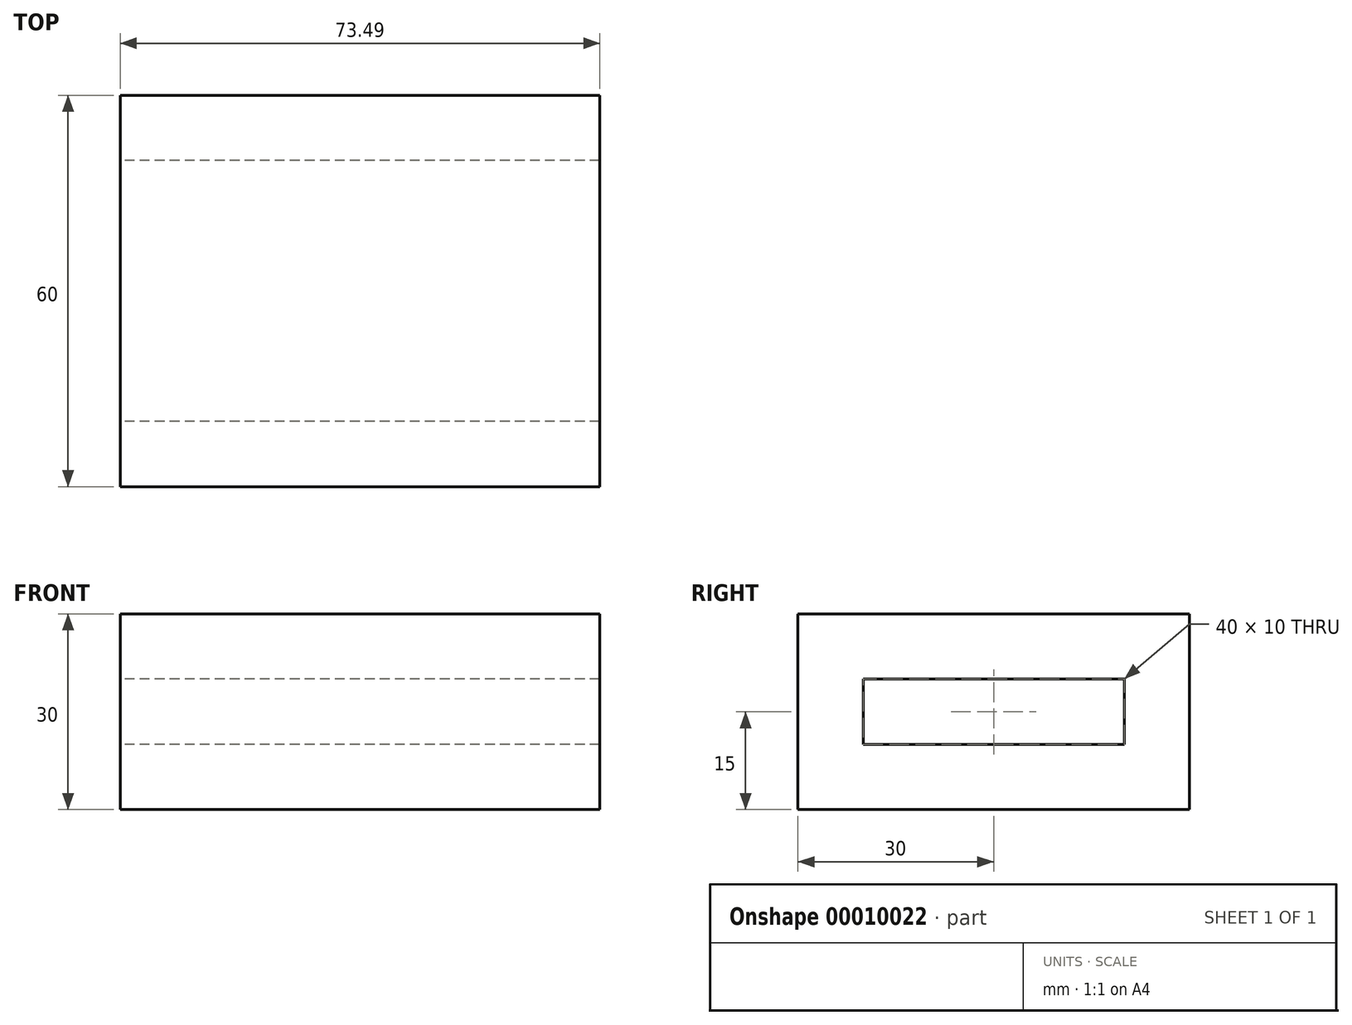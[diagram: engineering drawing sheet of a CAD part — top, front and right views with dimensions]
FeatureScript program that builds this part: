
annotation { "Feature Type Name" : "Feature", "Feature Type Description" : "" }
export const myFeature = defineFeature(function(context is Context, id is Id, definition is map)
    precondition{}
    {
        {
            var Q0;
            Q0=qCreatedBy(makeId("Right.planeOp"),FACE);
            var sketch = newSketch(context, id + "F0", { "sketchPlane" : qUnion([Q0])});
            skLineSegment(sketch, "E0.bottom", {"start": v(0, 0) * mm, "end": v(60, 0) * mm});
            skLineSegment(sketch, "E0.top", {"start": v(0, 30) * mm, "end": v(60, 30) * mm});
            skLineSegment(sketch, "E0.left", {"start": v(0, 0) * mm, "end": v(0, 30) * mm});
            skLineSegment(sketch, "E0.right", {"start": v(60, 0) * mm, "end": v(60, 30) * mm});
            skLineSegment(sketch, "E1.bottom", {"start": v(10, 20) * mm, "end": v(50, 20) * mm});
            skLineSegment(sketch, "E1.top", {"start": v(10, 10) * mm, "end": v(50, 10) * mm});
            skLineSegment(sketch, "E1.left", {"start": v(10, 20) * mm, "end": v(10, 10) * mm});
            skLineSegment(sketch, "E1.right", {"start": v(50, 20) * mm, "end": v(50, 10) * mm});
            skSolve(sketch);
        }
        {
            var Q0;
            Q0=makeQuery(id+"F0.imprint","IMPRINT",FACE,{"disambiguationData":[TD([[makeQuery(id+"F0.imprint","IMPRINT",EDGE,{"derivedFrom":sQuery(id+"F0.wireOp",EDGE,"E0.bottom")}),1.0]])]});
            extrude(context, id + "F1", {"entities" : qUnion([Q0]), "depth" : 30 * mm});
        }
        {
            var Q0;
            Q0 = qSketchRegion(id + "F0", true);
            var Q1;
            Q1=makeQuery(id+"F0.imprint","IMPRINT",FACE,{"disambiguationData":[TD([[makeQuery(id+"F0.imprint","IMPRINT",EDGE,{"derivedFrom":sQuery(id+"F0.wireOp",EDGE,"E1.bottom")}),-1.0]])]});
            extrude(context, id + "F2", {"entities" : qUnion([Q0, Q1]), "operationType" : NewBodyOperationType.ADD, "endBound" : BoundingType.THROUGH_ALL, "depth" : 25.4 * mm});
        }
        {
            var Q0;
            Q0=makeQuery(id+"F0.imprint","IMPRINT",FACE,{"disambiguationData":[TD([[makeQuery(id+"F0.imprint","IMPRINT",EDGE,{"derivedFrom":sQuery(id+"F0.wireOp",EDGE,"E1.bottom")}),-1.0]])]});
            extrude(context, id + "F3", {"entities" : qUnion([Q0]), "operationType" : NewBodyOperationType.REMOVE, "endBound" : BoundingType.THROUGH_ALL, "depth" : 25.4 * mm});
        }
    });
